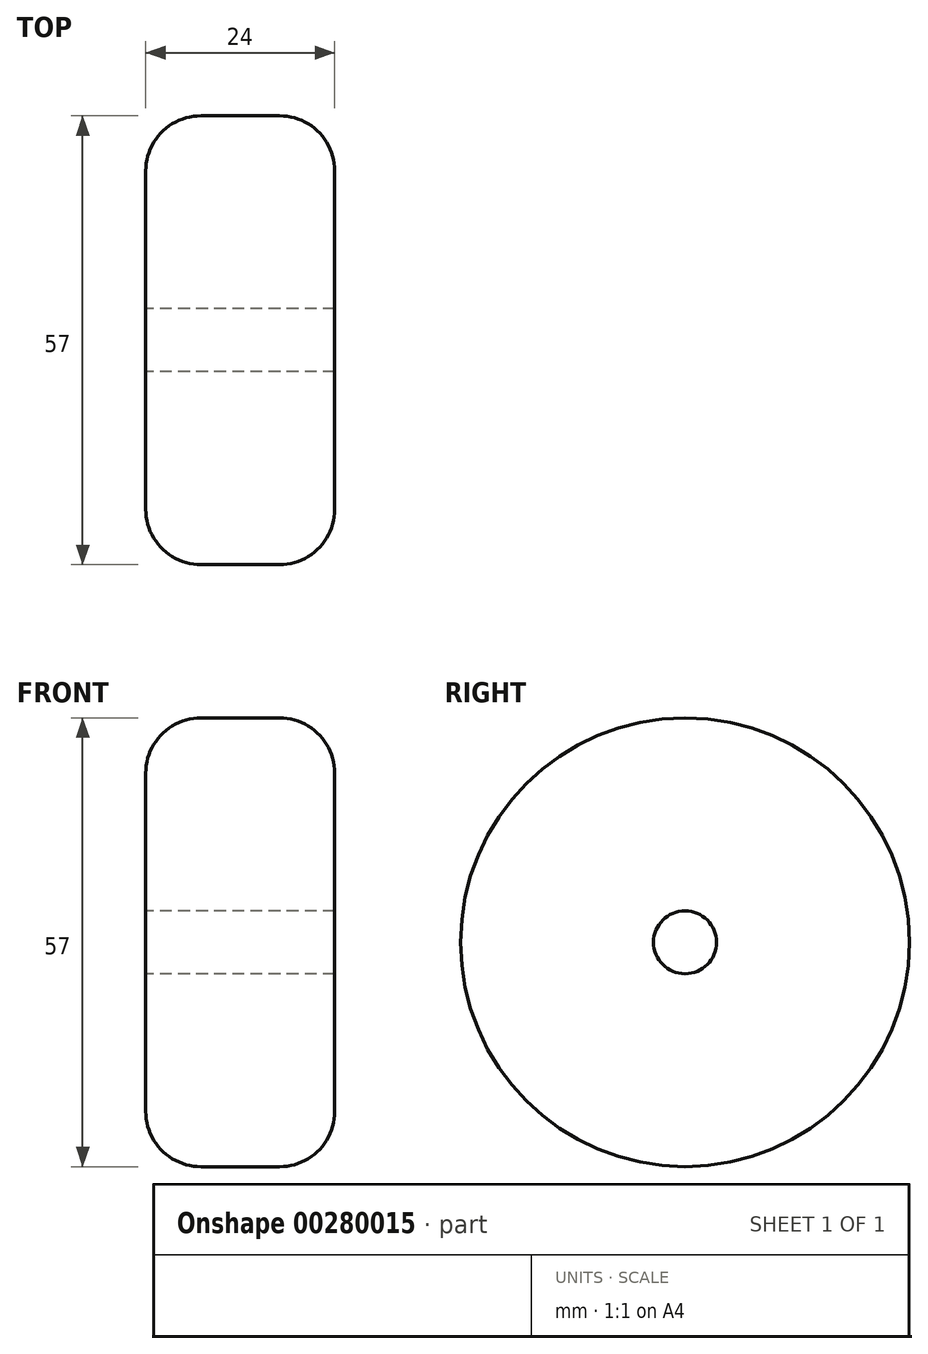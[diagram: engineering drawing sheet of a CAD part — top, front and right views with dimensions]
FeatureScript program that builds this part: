
annotation { "Feature Type Name" : "Feature", "Feature Type Description" : "" }
export const myFeature = defineFeature(function(context is Context, id is Id, definition is map)
    precondition{}
    {
        {
            var Q0;
            Q0=qCreatedBy(makeId("Front.planeOp"),FACE);
            var sketch = newSketch(context, id + "F0", { "sketchPlane" : qUnion([Q0])});
            skLineSegment(sketch, "E0.bottom", {"start": v(12, 0) * mm, "end": v(-12, 0) * mm});
            skLineSegment(sketch, "E0.top", {"start": v(5, 28.5) * mm, "end": v(-5, 28.5) * mm});
            skLineSegment(sketch, "E0.left", {"start": v(12, 0) * mm, "end": v(12, 21.5) * mm});
            skLineSegment(sketch, "E0.right", {"start": v(-12, 0) * mm, "end": v(-12, 21.5) * mm});
            skPoint(sketch, "E0.middle", {"position": v(0, 14.25) * mm});
            skPoint(sketch, "E1.visualSharp", {"position": v(-12, 28.5) * mm});
            skArc(sketch, "E1.filletArc", {"start": v(-5, 28.5) * mm, "mid": v(-9.95, 26.45) * mm, "end": v(-12, 21.5) * mm});
            skPoint(sketch, "E2.visualSharp", {"position": v(12, 28.5) * mm});
            skArc(sketch, "E2.filletArc", {"start": v(12, 21.5) * mm, "mid": v(9.95, 26.45) * mm, "end": v(5, 28.5) * mm});
            skLineSegment(sketch, "E3", {"start": v(-115.89, 0) * mm, "end": v(136.73, 0) * mm, "construction": true});
            skPoint(sketch, "E4", {"position": v(-12, 0) * mm});
            skPoint(sketch, "E5", {"position": v(12, 0) * mm});
            skSolve(sketch);
        }
        {
            var Q0;
            Q0 = qSketchRegion(id + "F0", true);
            var Q1;
            Q1=sQuery(id+"F0.wireOp",EDGE,"E3");
            revolve(context, id + "F1", {"entities" : qUnion([Q0]), "axis" : qUnion([Q1]), "revolveType" : RevolveType.FULL});
        }
        {
            var Q0;
            Q0=makeQuery(id+"F1.opRevolve","SWEPT_FACE",FACE,{"disambiguationData":[OSD([sQuery(id+"F0.wireOp",EDGE,"E0.right")])]});
            var sketch = newSketch(context, id + "F2", { "sketchPlane" : qUnion([Q0])});
            skPoint(sketch, "E6", {"position": v(0, 0) * mm});
            skLineSegment(sketch, "E7", {"start": v(-95.22, 0) * mm, "end": v(67.33, 0) * mm, "construction": true});
            skLineSegment(sketch, "E8", {"start": v(0, 51.5) * mm, "end": v(0, -72.85) * mm, "construction": true});
            skSolve(sketch);
        }
        {
            var Q0;
            Q0=sQuery(id+"F2.wireOp",VERTEX,"E6");
            var Q1;
            Q1=makeQuery(id+"F1.opRevolve","SWEPT_BODY",BODY,{"disambiguationData":[OSD([sQuery(id+"F0.wireOp",EDGE,"E0.bottom"),sQuery(id+"F0.wireOp",EDGE,"E0.top"),sQuery(id+"F0.wireOp",EDGE,"E0.left"),sQuery(id+"F0.wireOp",EDGE,"E0.right"),sQuery(id+"F0.wireOp",EDGE,"E1.filletArc"),sQuery(id+"F0.wireOp",EDGE,"E2.filletArc")])]});
            hole(context, id + "F3", {"style" : HoleStyle.SIMPLE, "endStyle" : HoleEndStyle.THROUGH, "holeDiameter" : 8 * mm, "tappedDepth" : 12 * mm, "tapClearance" : 3, "locations" : qUnion([Q0]), "scope" : qUnion([Q1])});
        }
    });
